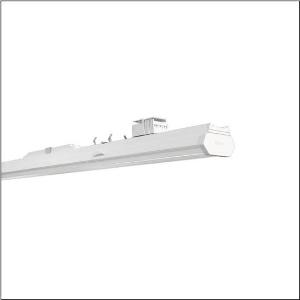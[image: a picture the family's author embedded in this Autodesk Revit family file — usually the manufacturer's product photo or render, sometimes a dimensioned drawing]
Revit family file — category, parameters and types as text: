
# Revit family: licross_r__21_protected_mo_52td1bvn48xg_aeae
name_source: partatom
category: Lighting Fixtures
units: mm (PartAtom-declared; Revit-internal decimal feet)

## family parameters
Cut with Voids When Loaded = No
Host = Face
Light Source = No
Part Type = Normal
Room Calculation Point = No
Round Connector Dimension = Use Diameter
Shared = No

## types (1)
- --- (1 x LED, 8000 lm, 48.3 W, 4000K)
    Apparent Load = 48 VA
    CIE Flux Codes = 54 82 95 97 100
    Color Rendering = 80
    Color Temperature = 4000K
    Default Elevation = 1800 mm
    Description = Licross® 21 Protected MO, luminaire insert, of sheet steel, galvanised, coil coated, white, length: 1.500mm, width: 90mm, height: 101mm, LED rated luminous flux: 8.000lm, light colour: 840, control gear: DALI 2, CLO, with plug, 5-pole, with phase selection, mains connection: 220..240V, AC, 50/60Hz, start of lifetime: 48W, end of service life: 58W, halogen-free wiring, primary optical cover: cover, of PMMA, light emission: direct distribution, primary light characteristic: symmetric, protection rating (complete): IP54, insulation class (complete): insulation class I (protective earthing), certification: CE, ENEC, VDE, UKCA, protection symbol: D if used in an environment with non-conductive dust loads with corresponding accessories, impact resistance: IK06, permissible ambient temperature for indoor applications: -25..+40°C, corresponds to IFS (International Featured Standards) requirements for safety and quality in the food industry, reducing of maximum allowable ambient temperature of 5°C with ceiling mounting, LABS conformity tested according to VDMA 24364:2018-05, packaging unit: 1 piece
    Height = 92 mm
    Lamp = 1 x LED
    Lamp Light Flux = 8000 lm
    Lamp Power = 48.3 W
    Lamp count = 1
    Length = 1500 mm
    Luminous efficacy = 166 lm/W
    Manufacturer = Siteco
    ModVariant = No
    Model = 52TD1BVN48XG
    Mounting Place = Ceiling
    Mounting Type = Pendant
    Number of Poles = 1
    OnlyDefault = Yes
    Power Factor = 1
    Product Name = Licross® 21 Protected MO
    Product group = luminaire insert
    ProductGroupID = 901
    Protection Class = Protection class I
    Protection Degree = IP 54
    RLX_Detail_Level = 1
    RLX_Emergency_Light_Flux = 0 lm
    RLX_Emergency_Type = 0
    RLX_Emergency_Type_DB = No
    RlxData = <blob elided: 24405 chars, md5=9b8b1456>
    Socket = socket
    Standby Power = 0 W
    System Light Flux = 8000 lm
    System Power = 48 W
    Type Comments = factory setting: luminous flux: 100 % | dim-lin: 254 | 326 mA
    Type Image = l_1256148.jpg
    URL = http://relux.com
    VarID = @adj_016537
    Voltage = 0 V
    Weight = 0.00 kg
    Width = 88 mm

## geometry (parser evidence)
native form markers: Blend x4, Sweep x11
no freeform markers — native parametric forms only
